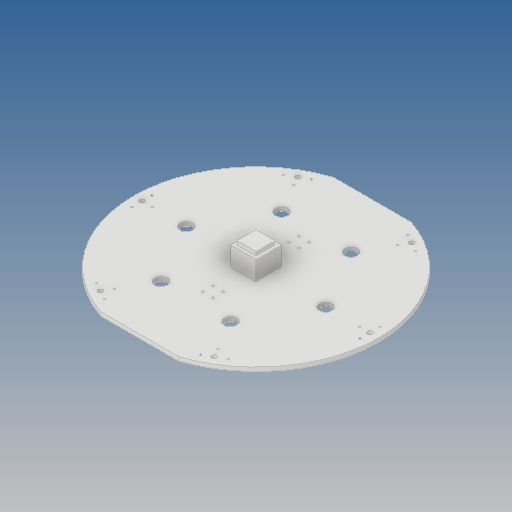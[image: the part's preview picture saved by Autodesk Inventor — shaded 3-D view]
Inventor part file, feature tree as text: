
AUTODESK INVENTOR PART (.ipt)
format: ipt  version: 2020 (Build 240168000, 168)  size: 679,936 bytes
history: native  units: mm
features: sketch x35, extrude x32, other x10, projected_geometry x6, hole x5, mirror x2, reference x2, revolve x1, loft x1, shell x1, fillet x1
ambient origin geometry x8: Origin, YZ Plane, XZ Plane, XY Plane, X Axis, Y Axis, Z Axis, Center Point
bodies: Body1 (feature_tree)
feature tree (96):
  revolve  "Вращение3"
  extrude  "Выдавливание106"  Depth=170.0mm
  extrude  "Выдавливание107"  Depth=100.0mm
  hole  "Отверстие2"  [1 undecoded]
  extrude  "Выдавливание108"  Depth=4.0mm
  hole  "Отверстие3"  [1 undecoded]
  hole  "Отверстие4"  [1 undecoded]
  hole  "Отверстие5"  [1 undecoded]
  hole  "Отверстие6"  [1 undecoded]
  extrude  "Выдавливание109"  Depth=130.0mm TaperAngle=0.0deg
  sketch  "Эскиз132"
  extrude  "Выдавливание110"  Depth=5.0mm
  extrude  "Выдавливание111"  Depth=2.0mm
  extrude  "Выдавливание113"  Depth=2.0mm
  extrude  "Выдавливание114"  Depth=2.0mm
  other  "РабПлоскость27"
  extrude  "Выдавливание115"  Depth=20.0mm
  extrude  "Выдавливание116"  Depth=10.0mm TaperAngle=0.0deg
  mirror  "Зеркальное отражение7"
  extrude  "Выдавливание117"  Depth=10.0mm TaperAngle=0.0deg
  extrude  "Выдавливание118"  Depth=143.802871mm
  sketch  "Эскиз4"
  other  "РабПлоскость1"
  sketch  "Эскиз5"
  loft  "Лофт1"
  extrude  "Выдавливание2"  Depth=1.0mm TaperAngle=0.0deg
  shell  "Оболочка1"  Thickness=5.0mm
  sketch  "Эскиз21"
  extrude  "Выдавливание15"  Depth=5.0mm
  extrude  "Выдавливание16"  Depth=2.0mm
  other  "РабПлоскость7"
  sketch  "Эскиз23"
  extrude  "Выдавливание17"  Depth=2.0mm
  extrude  "Выдавливание18"  Depth=5.0mm
  sketch  "Эскиз24"
  extrude  "Выдавливание19"  Depth=1.0mm TaperAngle=0.0deg
  extrude  "Выдавливание20"  Depth=3.0mm
  extrude  "Выдавливание21"  Depth=2.0mm
  mirror  "Зеркальное отражение2"
  other  "РабПлоскость12"
  sketch  "Эскиз42"
  extrude  "Выдавливание57"  Depth=6.0mm
  sketch  "Эскиз84"
  extrude  "Выдавливание75"  Depth=1.0mm TaperAngle=0.0deg
  extrude  "Выдавливание76"  Depth=2.0mm
  extrude  "Выдавливание77"  Depth=2.0mm
  extrude  "Выдавливание95"  Depth=2.0mm
  extrude  "Выдавливание96"  Depth=5.0mm
  extrude  "Выдавливание97"  Depth=1.0mm TaperAngle=0.0deg
  fillet  "Сопряжение3"  Radius=4.0mm
  extrude  "Выдавливание98"  Depth=2.0mm
  extrude  "Выдавливание101"  Depth=2.0mm
  other  "РабПлоскость25"
  extrude  "Выдавливание102"  Depth=2.0mm
  other  "РабПлоскость26"
  extrude  "Выдавливание103"  Depth=2.0mm
  extrude  "Выдавливание104"  Depth=16.0mm
  sketch  "Эскиз6"
  projected_geometry  "Спроецированная петля1"
  sketch  "Эскиз22"
  sketch  "Эскиз25"
  sketch  "Эскиз61"
  sketch  "Эскиз87"
  sketch  "Эскиз109"
  sketch  "Эскиз110"
  projected_geometry  "Спроецированная петля42"
  sketch  "Эскиз111"
  projected_geometry  "Спроецированная петля43"
  sketch  "Эскиз114"
  sketch  "Эскиз117"
  sketch  "Эскиз118"
  reference  "Ссылка1"
  reference  "Ссылка2"
  sketch  "Эскиз119"
  sketch  "Эскиз120"
  sketch  "Эскиз121"
  other  "Твердое тело3"
  sketch  "Эскиз124"
  sketch  "Эскиз125"
  sketch  "Эскиз126"
  sketch  "Эскиз127"
  sketch  "Эскиз129"
  sketch  "Эскиз130"
  sketch  "Эскиз131"
  projected_geometry  "Спроецированная петля45"
  projected_geometry  "Спроецированная петля46"
  sketch  "Эскиз133"
  sketch  "Эскиз134"
  sketch  "Эскиз135"
  sketch  "Эскиз136"
  projected_geometry  "Спроецированная петля47"
  sketch  "Эскиз137"
  sketch  "Эскиз138"
  other  "<userpath>\Desktop\САПР\Работы\ПД\робот\робот - сборка фулл.iam"
  other  "робот - сборка фулл.iam"
  other  "крепление-стенки:1"
note: 5 required parameter values undecoded (feature->parameter linkage not recoverable at this tier; creation-order binding heuristic only, values carry confidence <= 0.55)
